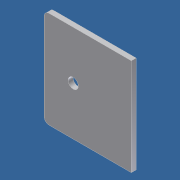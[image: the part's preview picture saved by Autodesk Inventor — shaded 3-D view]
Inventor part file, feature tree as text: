
AUTODESK INVENTOR PART (.ipt)
format: ipt  version: unknown  size: 174,592 bytes
history: native  units: in
note: dims shown in document units (in); Inventor stores cm internally (conversion verified against a paired STEP export)
features: extrude x1, fillet x1, hole x1, sketch x1
ambient origin geometry x8: Origin, YZ Plane, XZ Plane, XY Plane, X Axis, Y Axis, Z Axis, Center Point
bodies: Solid1 (feature_tree)
feature tree (4):
  extrude  "Extrusion1"  Depth=0.125in TaperAngle=0.0deg
  fillet  "Fillet1"  Radius=0.125in
  hole  "Hole1"  [1 undecoded]
  sketch  "Sketch1"  dims[d0=2.25in d1=0.125in d2=0.0in d3=0.125in d4=0.75in d5=1.25in d6=0.265in d7=0.75in d8=0.375in d9=0.25in d10=0.5635in d11=1.0in d12=0.8108in d13=2.5in]
note: 1 required parameter value undecoded (feature->parameter linkage not recoverable at this tier; creation-order binding heuristic only, values carry confidence <= 0.55)
